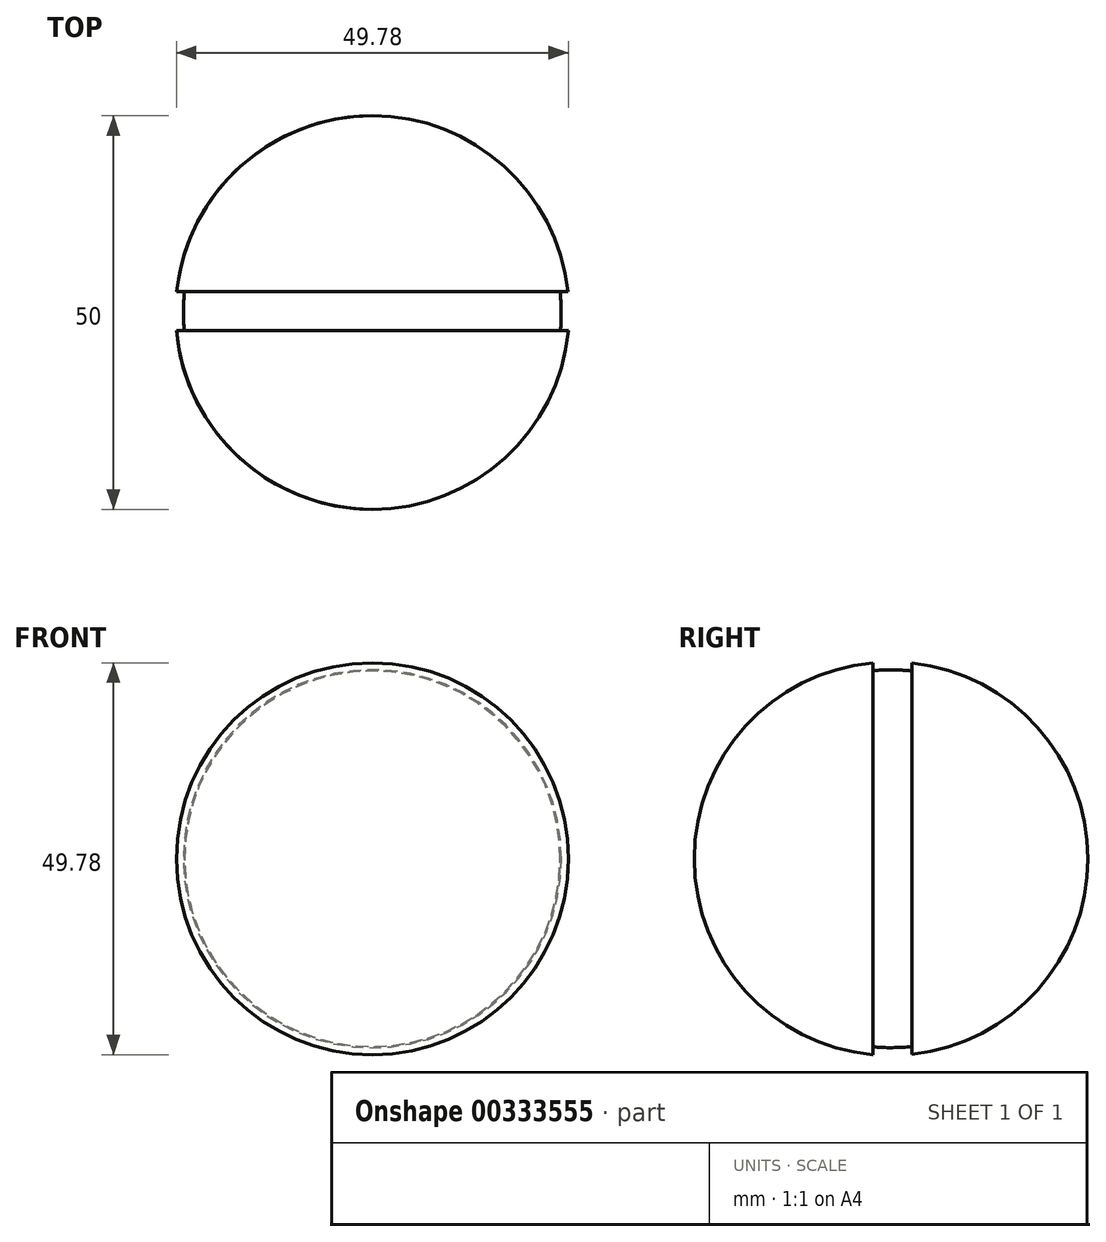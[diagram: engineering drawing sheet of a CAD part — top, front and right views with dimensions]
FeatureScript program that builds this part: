
annotation { "Feature Type Name" : "Feature", "Feature Type Description" : "" }
export const myFeature = defineFeature(function(context is Context, id is Id, definition is map)
    precondition{}
    {
        {
            var Q0;
            Q0=qCreatedBy(makeId("Top.planeOp"),FACE);
            var sketch = newSketch(context, id + "F0", { "sketchPlane" : qUnion([Q0])});
            skArc(sketch, "E0", {"start": v(0, 25) * mm, "mid": v(-16.7, 18.6) * mm, "end": v(-24.86, 2.68) * mm});
            skArc(sketch, "E1", {"start": v(-23.85, 2.68) * mm, "mid": v(-24, 0.18) * mm, "end": v(-23.89, -2.32) * mm});
            skLineSegment(sketch, "E2.bottom", {"start": v(-23.85, 2.68) * mm, "end": v(-24.86, 2.68) * mm});
            skLineSegment(sketch, "E2.top", {"start": v(-23.89, -2.32) * mm, "end": v(-24.9, -2.32) * mm});
            skLineSegment(sketch, "E3", {"start": v(0, 25) * mm, "end": v(0, -25) * mm});
            skArc(sketch, "E4.trimOffspring", {"start": v(-24.9, -2.32) * mm, "mid": v(-16.84, -18.48) * mm, "end": v(0, -25) * mm});
            skSolve(sketch);
        }
        {
            var Q0;
            Q0=makeQuery(id+"F0.imprint","IMPRINT",FACE,{"disambiguationData":[TD([[makeQuery(id+"F0.imprint","IMPRINT",EDGE,{"derivedFrom":sQuery(id+"F0.wireOp",EDGE,"E0")}),1.0]])]});
            var Q1;
            Q1=sQuery(id+"F0.wireOp",EDGE,"E3");
            revolve(context, id + "F1", {"entities" : qUnion([Q0]), "axis" : qUnion([Q1]), "revolveType" : RevolveType.FULL});
        }
    });
